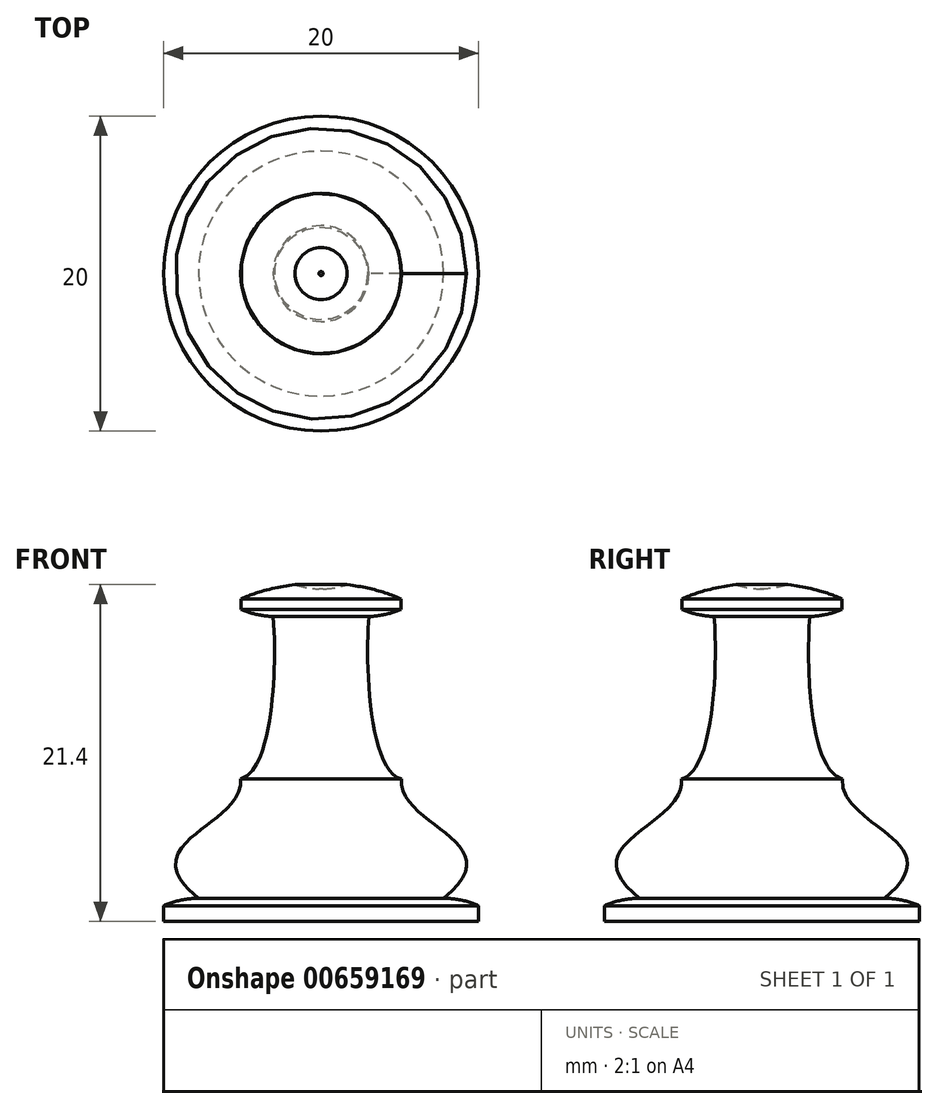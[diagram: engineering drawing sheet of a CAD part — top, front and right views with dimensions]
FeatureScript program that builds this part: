
annotation { "Feature Type Name" : "Feature", "Feature Type Description" : "" }
export const myFeature = defineFeature(function(context is Context, id is Id, definition is map)
    precondition{}
    {
        {
            var Q0;
            Q0=qCreatedBy(makeId("Front.planeOp"),FACE);
            var sketch = newSketch(context, id + "F0", { "sketchPlane" : qUnion([Q0])});
            skLineSegment(sketch, "E0", {"start": v(0, 0) * mm, "end": v(-10, 0) * mm});
            skLineSegment(sketch, "E1", {"start": v(-10, 0) * mm, "end": v(-10, 1) * mm});
            skFitSpline(sketch, "E2", {"points": [v(-10, 1) * mm, v(-7.78, 1.47) * mm], "startDerivative": vector(2.05, 0.95) * mm, "endDerivative": vector(2.28, 0.04) * mm});
            skFitSpline(sketch, "E3", {"points": [v(-7.78, 1.47) * mm, v(-5.1, 9.05) * mm], "startDerivative": vector(-13.53, 11.02) * mm, "endDerivative": vector(-0.47, 9.31) * mm});
            skFitSpline(sketch, "E4", {"points": [v(-5.1, 9.05) * mm, v(-3.04, 19.37) * mm], "startDerivative": vector(6.43, 1.67) * mm, "endDerivative": vector(-0.74, 7.77) * mm});
            skFitSpline(sketch, "E5", {"points": [v(-3.04, 19.37) * mm, v(-5.08, 19.83) * mm], "startDerivative": vector(-2, 0.1) * mm, "endDerivative": vector(-2.08, 0.93) * mm});
            skLineSegment(sketch, "E6", {"start": v(-5.08, 19.83) * mm, "end": v(-5.08, 20.49) * mm});
            skFitSpline(sketch, "E7", {"points": [v(-5.08, 20.49) * mm, v(-1.66, 21.4) * mm], "startDerivative": vector(3.6, 1.5) * mm, "endDerivative": vector(4.29, 0.62) * mm});
            skLineSegment(sketch, "E8", {"start": v(0, 30.62) * mm, "end": v(0, 0) * mm});
            skArc(sketch, "E9", {"start": v(0, 30.62) * mm, "mid": v(-4.74, 26.71) * mm, "end": v(-1.66, 21.4) * mm});
            skSolve(sketch);
        }
        {
            var Q0;
            Q0=makeQuery(id+"F0.imprint","IMPRINT",FACE,{"disambiguationData":[TD([[makeQuery(id+"F0.imprint","IMPRINT",EDGE,{"derivedFrom":sQuery(id+"F0.wireOp",EDGE,"E0")}),-1.0]])]});
            var Q1;
            Q1=sQuery(id+"F0.wireOp",EDGE,"E8");
            revolve(context, id + "F1", {"entities" : qUnion([Q0]), "axis" : qUnion([Q1]), "revolveType" : RevolveType.FULL});
        }
    });
